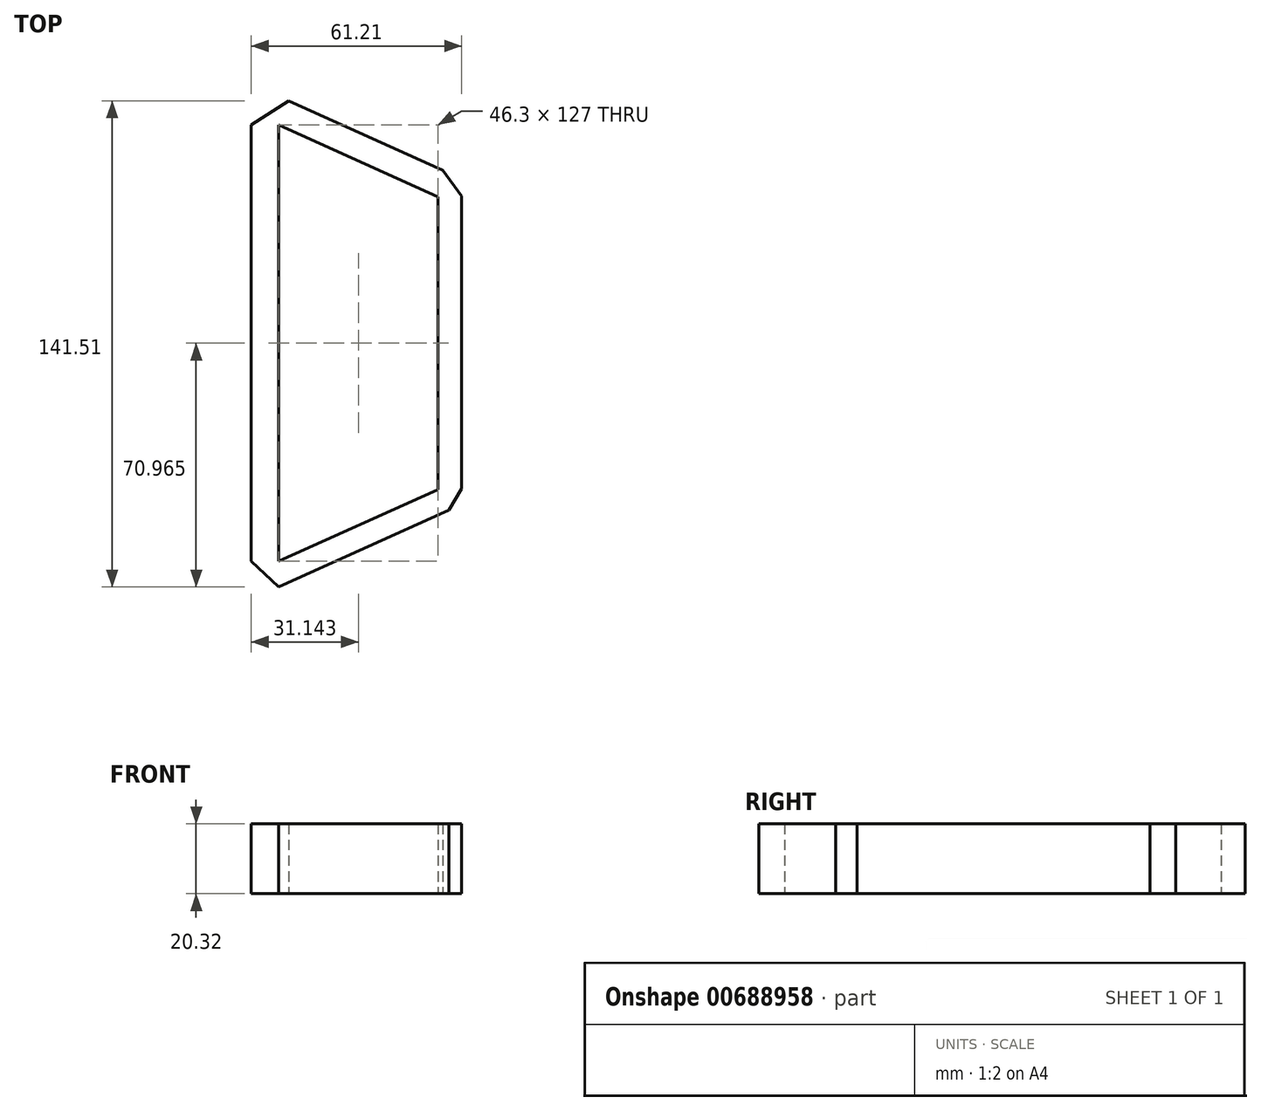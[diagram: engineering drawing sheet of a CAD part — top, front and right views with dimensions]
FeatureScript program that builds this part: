
annotation { "Feature Type Name" : "Feature", "Feature Type Description" : "" }
export const myFeature = defineFeature(function(context is Context, id is Id, definition is map)
    precondition{}
    {
        {
            var Q0;
            Q0=qCreatedBy(makeId("Top.planeOp"),FACE);
            var sketch = newSketch(context, id + "F0", { "sketchPlane" : qUnion([Q0])});
            skLineSegment(sketch, "E0", {"start": v(-29.62, 69.45) * mm, "end": v(-29.62, -57.55) * mm});
            skLineSegment(sketch, "E1", {"start": v(-29.62, 69.45) * mm, "end": v(16.68, 48.54) * mm});
            skLineSegment(sketch, "E2", {"start": v(-29.62, -57.55) * mm, "end": v(16.68, -36.65) * mm});
            skLineSegment(sketch, "E3", {"start": v(16.68, 48.54) * mm, "end": v(16.68, -36.65) * mm});
            skLineSegment(sketch, "E4", {"start": v(-26.7, 76.5) * mm, "end": v(18.14, 56.24) * mm});
            skLineSegment(sketch, "E5", {"start": v(23.6, 48.78) * mm, "end": v(23.6, -36.43) * mm});
            skLineSegment(sketch, "E6", {"start": v(18.14, 56.24) * mm, "end": v(23.6, 48.78) * mm});
            skLineSegment(sketch, "E7", {"start": v(-37.61, 69.45) * mm, "end": v(-37.61, -57.55) * mm});
            skLineSegment(sketch, "E8", {"start": v(-37.61, 69.45) * mm, "end": v(-26.7, 76.5) * mm});
            skLineSegment(sketch, "E9", {"start": v(-29.62, -65.02) * mm, "end": v(19.9, -42.66) * mm});
            skLineSegment(sketch, "E10", {"start": v(19.9, -42.66) * mm, "end": v(23.6, -36.43) * mm});
            skLineSegment(sketch, "E11", {"start": v(-29.62, -65.02) * mm, "end": v(-37.61, -57.55) * mm});
            skSolve(sketch);
        }
        {
            var Q0;
            Q0=makeQuery(id+"F0.imprint","IMPRINT",FACE,{"disambiguationData":[TD([[makeQuery(id+"F0.imprint","IMPRINT",EDGE,{"derivedFrom":sQuery(id+"F0.wireOp",EDGE,"E0")}),-1.0]])]});
            extrude(context, id + "F1", {"entities" : qUnion([Q0]), "endBound" : BoundingType.SYMMETRIC, "depth" : 20.32 * mm, "offsetDistance" : 25.4 * mm});
        }
    });
